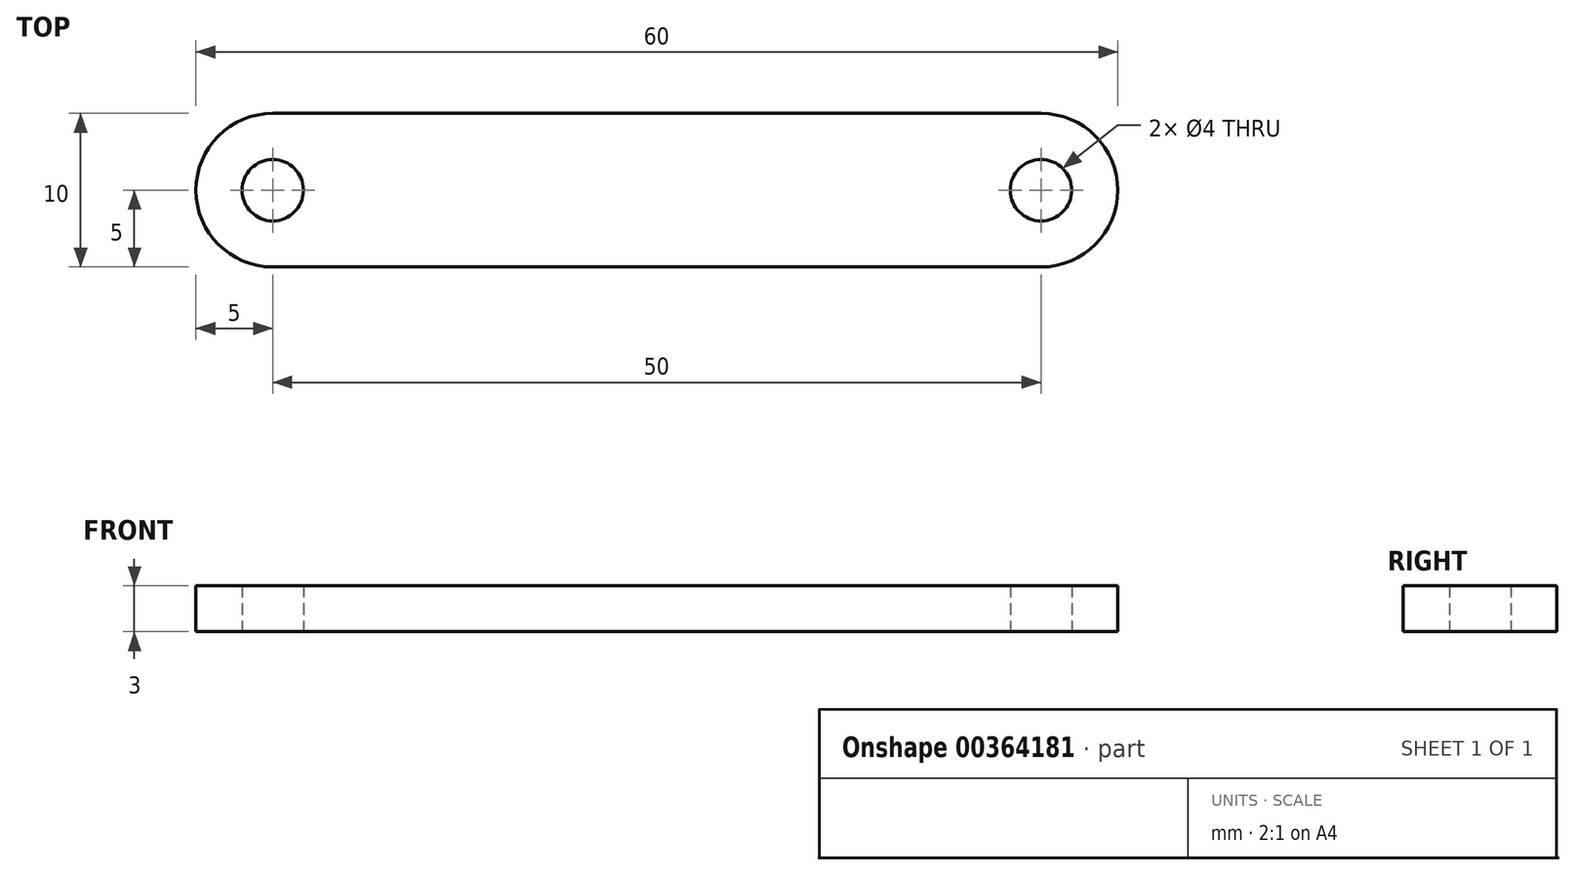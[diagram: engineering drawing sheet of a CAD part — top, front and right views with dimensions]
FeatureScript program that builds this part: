
annotation { "Feature Type Name" : "Feature", "Feature Type Description" : "" }
export const myFeature = defineFeature(function(context is Context, id is Id, definition is map)
    precondition{}
    {
        {
            var Q0;
            Q0=qCreatedBy(makeId("Top.planeOp"),FACE);
            var sketch = newSketch(context, id + "F0", { "sketchPlane" : qUnion([Q0])});
            skLineSegment(sketch, "E0.bottom", {"start": v(25, 5) * mm, "end": v(-25, 5) * mm});
            skLineSegment(sketch, "E0.top", {"start": v(25, -5) * mm, "end": v(-25, -5) * mm});
            skPoint(sketch, "E0.middle", {"position": v(0, 0) * mm});
            skCircle(sketch, "E1", {"center": v(-25, 0) * mm, "radius": 2 * mm});
            skCircle(sketch, "E2", {"center": v(25, 0) * mm, "radius": 2 * mm});
            skArc(sketch, "E3", {"start": v(-25, 5) * mm, "mid": v(-30, 0) * mm, "end": v(-25, -5) * mm});
            skArc(sketch, "E4", {"start": v(25, -5) * mm, "mid": v(30, 0) * mm, "end": v(25, 5) * mm});
            skSolve(sketch);
        }
        {
            var Q0;
            Q0=qSketchRegion(id+"F0",true);
            extrude(context, id + "F1", {"entities" : qUnion([Q0]), "depth" : 3 * mm});
        }
    });
